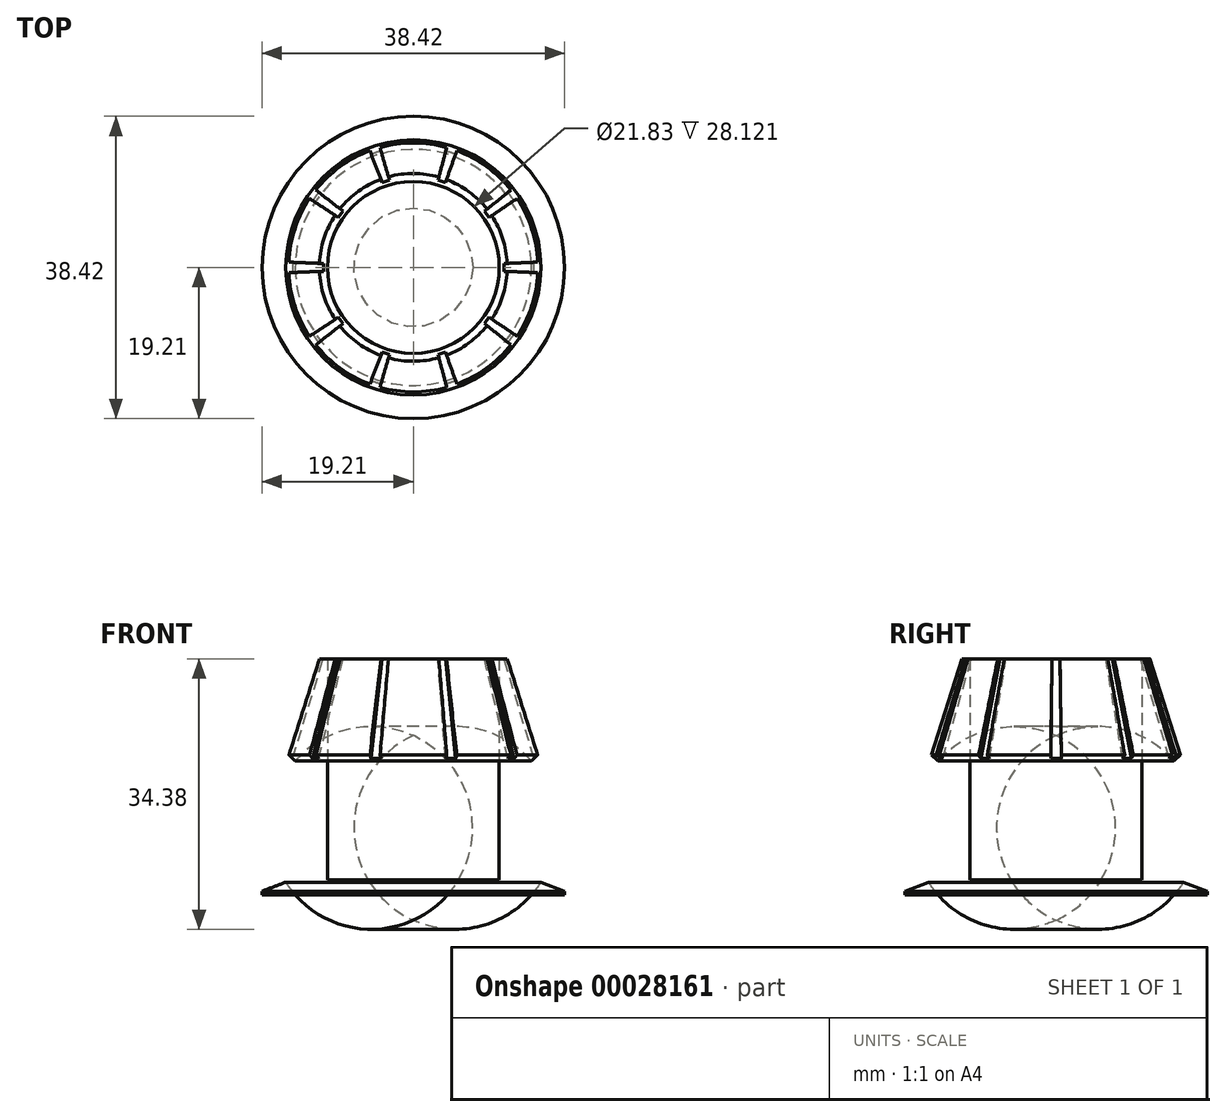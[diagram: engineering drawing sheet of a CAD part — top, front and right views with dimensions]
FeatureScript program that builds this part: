
annotation { "Feature Type Name" : "Feature", "Feature Type Description" : "" }
export const myFeature = defineFeature(function(context is Context, id is Id, definition is map)
    precondition{}
    {
        {
            var Q0;
            Q0=qCreatedBy(makeId("Front.planeOp"),FACE);
            var sketch = newSketch(context, id + "F0", { "sketchPlane" : qUnion([Q0])});
            skLineSegment(sketch, "E0", {"start": v(0, 0) * mm, "end": v(0, 30) * mm});
            skLineSegment(sketch, "E1", {"start": v(0, 0) * mm, "end": v(15, 0) * mm});
            skLineSegment(sketch, "E2", {"start": v(15, 0) * mm, "end": v(15, 17) * mm});
            skArc(sketch, "E3", {"start": v(15, 0) * mm, "mid": v(18.2, 8.5) * mm, "end": v(15, 17) * mm});
            skLineSegment(sketch, "E4", {"start": v(16.2, 1.6) * mm, "end": v(19.2, 0.46) * mm});
            skLineSegment(sketch, "E5", {"start": v(19.2, 0.46) * mm, "end": v(19.2, 0) * mm});
            skLineSegment(sketch, "E6", {"start": v(19.2, 0) * mm, "end": v(15, 0) * mm});
            skLineSegment(sketch, "E7", {"start": v(15, 17) * mm, "end": v(15.81, 17.76) * mm});
            skLineSegment(sketch, "E8", {"start": v(15.81, 17.76) * mm, "end": v(11.93, 30) * mm});
            skLineSegment(sketch, "E9", {"start": v(11.93, 30) * mm, "end": v(10.91, 30) * mm});
            skLineSegment(sketch, "E10", {"start": v(10.91, 30) * mm, "end": v(10.91, 1.88) * mm});
            skLineSegment(sketch, "E11", {"start": v(10.91, 1.88) * mm, "end": v(0, 1.88) * mm});
            skSolve(sketch);
        }
        {
            var Q0;
            Q0 = qSketchRegion(id + "F0", true);
            var Q1;
            Q1=sQuery(id+"F0.wireOp",EDGE,"E0");
            revolve(context, id + "F1", {"entities" : qUnion([Q0]), "axis" : qUnion([Q1]), "revolveType" : RevolveType.FULL});
        }
        {
            var Q0;
            Q0=makeQuery(id+"F1.opRevolve","SWEPT_FACE",FACE,{"disambiguationData":[OSD([sQuery(id+"F0.wireOp",EDGE,"E9")])]});
            var sketch = newSketch(context, id + "F2", { "sketchPlane" : qUnion([Q0])});
            skLineSegment(sketch, "E12.rect.bottom", {"start": v(12.33, 0.5) * mm, "end": v(11.53, 0.5) * mm});
            skLineSegment(sketch, "E12.rect.top", {"start": v(12.33, -0.5) * mm, "end": v(11.53, -0.5) * mm});
            skLineSegment(sketch, "E12.rect.left", {"start": v(12.33, 0.5) * mm, "end": v(12.33, -0.5) * mm});
            skLineSegment(sketch, "E12.rect.right", {"start": v(11.53, 0.5) * mm, "end": v(11.53, -0.5) * mm});
            skPoint(sketch, "E12.rect.middle", {"position": v(11.93, 0) * mm});
            skPoint(sketch, "E13.1.0", {"position": v(9.66, 6.98) * mm});
            skLineSegment(sketch, "E13.1.1", {"start": v(9.68, 7.63) * mm, "end": v(9.04, 7.16) * mm});
            skLineSegment(sketch, "E13.1.2", {"start": v(10.28, 6.8) * mm, "end": v(9.64, 6.33) * mm});
            skLineSegment(sketch, "E13.1.3", {"start": v(9.68, 7.63) * mm, "end": v(10.28, 6.8) * mm});
            skLineSegment(sketch, "E13.1.4", {"start": v(9.04, 7.16) * mm, "end": v(9.64, 6.33) * mm});
            skPoint(sketch, "E13.2.0", {"position": v(3.72, 11.3) * mm});
            skLineSegment(sketch, "E13.2.1", {"start": v(3.36, 11.83) * mm, "end": v(3.11, 11.07) * mm});
            skLineSegment(sketch, "E13.2.2", {"start": v(4.33, 11.52) * mm, "end": v(4.08, 10.76) * mm});
            skLineSegment(sketch, "E13.2.3", {"start": v(3.36, 11.83) * mm, "end": v(4.33, 11.52) * mm});
            skLineSegment(sketch, "E13.2.4", {"start": v(3.11, 11.07) * mm, "end": v(4.08, 10.76) * mm});
            skPoint(sketch, "E13.3.0", {"position": v(-3.62, 11.3) * mm});
            skLineSegment(sketch, "E13.3.1", {"start": v(-4.23, 11.52) * mm, "end": v(-3.98, 10.76) * mm});
            skLineSegment(sketch, "E13.3.2", {"start": v(-3.26, 11.83) * mm, "end": v(-3.01, 11.07) * mm});
            skLineSegment(sketch, "E13.3.3", {"start": v(-4.23, 11.52) * mm, "end": v(-3.26, 11.83) * mm});
            skLineSegment(sketch, "E13.3.4", {"start": v(-3.98, 10.76) * mm, "end": v(-3.01, 11.07) * mm});
            skPoint(sketch, "E13.4.0", {"position": v(-9.56, 6.98) * mm});
            skLineSegment(sketch, "E13.4.1", {"start": v(-10.18, 6.8) * mm, "end": v(-9.53, 6.33) * mm});
            skLineSegment(sketch, "E13.4.2", {"start": v(-9.58, 7.63) * mm, "end": v(-8.93, 7.16) * mm});
            skLineSegment(sketch, "E13.4.3", {"start": v(-10.18, 6.8) * mm, "end": v(-9.58, 7.63) * mm});
            skLineSegment(sketch, "E13.4.4", {"start": v(-9.53, 6.33) * mm, "end": v(-8.93, 7.16) * mm});
            skPoint(sketch, "E13.5.0", {"position": v(-11.83, 0) * mm});
            skLineSegment(sketch, "E13.5.1", {"start": v(-12.23, -0.5) * mm, "end": v(-11.43, -0.5) * mm});
            skLineSegment(sketch, "E13.5.2", {"start": v(-12.23, 0.5) * mm, "end": v(-11.43, 0.5) * mm});
            skLineSegment(sketch, "E13.5.3", {"start": v(-12.23, -0.5) * mm, "end": v(-12.23, 0.5) * mm});
            skLineSegment(sketch, "E13.5.4", {"start": v(-11.43, -0.5) * mm, "end": v(-11.43, 0.5) * mm});
            skPoint(sketch, "E13.6.0", {"position": v(-9.56, -6.98) * mm});
            skLineSegment(sketch, "E13.6.1", {"start": v(-9.58, -7.63) * mm, "end": v(-8.93, -7.16) * mm});
            skLineSegment(sketch, "E13.6.2", {"start": v(-10.18, -6.8) * mm, "end": v(-9.53, -6.33) * mm});
            skLineSegment(sketch, "E13.6.3", {"start": v(-9.58, -7.63) * mm, "end": v(-10.18, -6.8) * mm});
            skLineSegment(sketch, "E13.6.4", {"start": v(-8.93, -7.16) * mm, "end": v(-9.53, -6.33) * mm});
            skPoint(sketch, "E13.7.0", {"position": v(-3.62, -11.3) * mm});
            skLineSegment(sketch, "E13.7.1", {"start": v(-3.26, -11.83) * mm, "end": v(-3.01, -11.07) * mm});
            skLineSegment(sketch, "E13.7.2", {"start": v(-4.23, -11.52) * mm, "end": v(-3.98, -10.76) * mm});
            skLineSegment(sketch, "E13.7.3", {"start": v(-3.26, -11.83) * mm, "end": v(-4.23, -11.52) * mm});
            skLineSegment(sketch, "E13.7.4", {"start": v(-3.01, -11.07) * mm, "end": v(-3.98, -10.76) * mm});
            skPoint(sketch, "E13.8.0", {"position": v(3.72, -11.3) * mm});
            skLineSegment(sketch, "E13.8.1", {"start": v(4.33, -11.52) * mm, "end": v(4.08, -10.76) * mm});
            skLineSegment(sketch, "E13.8.2", {"start": v(3.36, -11.83) * mm, "end": v(3.11, -11.07) * mm});
            skLineSegment(sketch, "E13.8.3", {"start": v(4.33, -11.52) * mm, "end": v(3.36, -11.83) * mm});
            skLineSegment(sketch, "E13.8.4", {"start": v(4.08, -10.76) * mm, "end": v(3.11, -11.07) * mm});
            skPoint(sketch, "E13.9.0", {"position": v(9.66, -6.98) * mm});
            skLineSegment(sketch, "E13.9.1", {"start": v(10.28, -6.8) * mm, "end": v(9.64, -6.33) * mm});
            skLineSegment(sketch, "E13.9.2", {"start": v(9.68, -7.63) * mm, "end": v(9.04, -7.16) * mm});
            skLineSegment(sketch, "E13.9.3", {"start": v(10.28, -6.8) * mm, "end": v(9.68, -7.63) * mm});
            skLineSegment(sketch, "E13.9.4", {"start": v(9.64, -6.33) * mm, "end": v(9.04, -7.16) * mm});
            skPoint(sketch, "E13.center", {"position": v(0.05, 0) * mm});
            skSolve(sketch);
        }
        {
            var Q0;
            Q0=qCreatedBy(makeId("Top.planeOp"),FACE);
            cPlane(context, id + "F3", {"entities" : qUnion([Q0]), "cplaneType" : CPlaneType.OFFSET, "offset" : 17 * mm, "width" : 150 * mm, "height" : 150 * mm});
        }
        {
            var Q0;
            Q0=qCreatedBy(id+"F3.planeOp",FACE);
            var sketch = newSketch(context, id + "F4", { "sketchPlane" : qUnion([Q0])});
            skLineSegment(sketch, "E14.rect.bottom", {"start": v(15.44, 0.68) * mm, "end": v(16.24, 0.68) * mm});
            skLineSegment(sketch, "E14.rect.top", {"start": v(15.44, -0.68) * mm, "end": v(16.24, -0.68) * mm});
            skLineSegment(sketch, "E14.rect.left", {"start": v(15.44, 0.68) * mm, "end": v(15.44, -0.68) * mm});
            skLineSegment(sketch, "E14.rect.right", {"start": v(16.24, 0.68) * mm, "end": v(16.24, -0.68) * mm});
            skPoint(sketch, "E14.rect.middle", {"position": v(15.84, 0) * mm});
            skLineSegment(sketch, "E15.1.0", {"start": v(12.09, 9.63) * mm, "end": v(12.73, 10.1) * mm});
            skLineSegment(sketch, "E15.1.1", {"start": v(12.89, 8.52) * mm, "end": v(13.54, 9) * mm});
            skLineSegment(sketch, "E15.1.2", {"start": v(12.09, 9.63) * mm, "end": v(12.89, 8.52) * mm});
            skLineSegment(sketch, "E15.1.3", {"start": v(12.73, 10.1) * mm, "end": v(13.54, 9) * mm});
            skPoint(sketch, "E15.1.8", {"position": v(12.81, 9.3) * mm});
            skLineSegment(sketch, "E15.2.0", {"start": v(4.12, 14.9) * mm, "end": v(4.37, 15.65) * mm});
            skLineSegment(sketch, "E15.2.1", {"start": v(5.42, 14.47) * mm, "end": v(5.67, 15.23) * mm});
            skLineSegment(sketch, "E15.2.2", {"start": v(4.12, 14.9) * mm, "end": v(5.42, 14.47) * mm});
            skLineSegment(sketch, "E15.2.3", {"start": v(4.37, 15.65) * mm, "end": v(5.67, 15.23) * mm});
            skPoint(sketch, "E15.2.8", {"position": v(4.9, 15.06) * mm});
            skLineSegment(sketch, "E15.3.0", {"start": v(-5.42, 14.47) * mm, "end": v(-5.67, 15.23) * mm});
            skLineSegment(sketch, "E15.3.1", {"start": v(-4.12, 14.9) * mm, "end": v(-4.37, 15.65) * mm});
            skLineSegment(sketch, "E15.3.2", {"start": v(-5.42, 14.47) * mm, "end": v(-4.12, 14.9) * mm});
            skLineSegment(sketch, "E15.3.3", {"start": v(-5.67, 15.23) * mm, "end": v(-4.37, 15.65) * mm});
            skPoint(sketch, "E15.3.8", {"position": v(-4.9, 15.06) * mm});
            skLineSegment(sketch, "E15.4.0", {"start": v(-12.89, 8.52) * mm, "end": v(-13.54, 9) * mm});
            skLineSegment(sketch, "E15.4.1", {"start": v(-12.09, 9.63) * mm, "end": v(-12.73, 10.1) * mm});
            skLineSegment(sketch, "E15.4.2", {"start": v(-12.89, 8.52) * mm, "end": v(-12.09, 9.63) * mm});
            skLineSegment(sketch, "E15.4.3", {"start": v(-13.54, 9) * mm, "end": v(-12.73, 10.1) * mm});
            skPoint(sketch, "E15.4.8", {"position": v(-12.81, 9.3) * mm});
            skLineSegment(sketch, "E15.5.0", {"start": v(-15.44, -0.68) * mm, "end": v(-16.24, -0.68) * mm});
            skLineSegment(sketch, "E15.5.1", {"start": v(-15.44, 0.68) * mm, "end": v(-16.24, 0.68) * mm});
            skLineSegment(sketch, "E15.5.2", {"start": v(-15.44, -0.68) * mm, "end": v(-15.44, 0.68) * mm});
            skLineSegment(sketch, "E15.5.3", {"start": v(-16.24, -0.68) * mm, "end": v(-16.24, 0.68) * mm});
            skPoint(sketch, "E15.5.8", {"position": v(-15.84, 0) * mm});
            skLineSegment(sketch, "E15.6.0", {"start": v(-12.09, -9.63) * mm, "end": v(-12.73, -10.1) * mm});
            skLineSegment(sketch, "E15.6.1", {"start": v(-12.89, -8.52) * mm, "end": v(-13.54, -9) * mm});
            skLineSegment(sketch, "E15.6.2", {"start": v(-12.09, -9.63) * mm, "end": v(-12.89, -8.52) * mm});
            skLineSegment(sketch, "E15.6.3", {"start": v(-12.73, -10.1) * mm, "end": v(-13.54, -9) * mm});
            skPoint(sketch, "E15.6.8", {"position": v(-12.81, -9.3) * mm});
            skLineSegment(sketch, "E15.7.0", {"start": v(-4.12, -14.9) * mm, "end": v(-4.37, -15.65) * mm});
            skLineSegment(sketch, "E15.7.1", {"start": v(-5.42, -14.47) * mm, "end": v(-5.67, -15.23) * mm});
            skLineSegment(sketch, "E15.7.2", {"start": v(-4.12, -14.9) * mm, "end": v(-5.42, -14.47) * mm});
            skLineSegment(sketch, "E15.7.3", {"start": v(-4.37, -15.65) * mm, "end": v(-5.67, -15.23) * mm});
            skPoint(sketch, "E15.7.8", {"position": v(-4.9, -15.06) * mm});
            skLineSegment(sketch, "E15.8.0", {"start": v(5.42, -14.47) * mm, "end": v(5.67, -15.23) * mm});
            skLineSegment(sketch, "E15.8.1", {"start": v(4.12, -14.9) * mm, "end": v(4.37, -15.65) * mm});
            skLineSegment(sketch, "E15.8.2", {"start": v(5.42, -14.47) * mm, "end": v(4.12, -14.9) * mm});
            skLineSegment(sketch, "E15.8.3", {"start": v(5.67, -15.23) * mm, "end": v(4.37, -15.65) * mm});
            skPoint(sketch, "E15.8.8", {"position": v(4.9, -15.06) * mm});
            skLineSegment(sketch, "E15.9.0", {"start": v(12.89, -8.52) * mm, "end": v(13.54, -9) * mm});
            skLineSegment(sketch, "E15.9.1", {"start": v(12.09, -9.63) * mm, "end": v(12.73, -10.1) * mm});
            skLineSegment(sketch, "E15.9.2", {"start": v(12.89, -8.52) * mm, "end": v(12.09, -9.63) * mm});
            skLineSegment(sketch, "E15.9.3", {"start": v(13.54, -9) * mm, "end": v(12.73, -10.1) * mm});
            skPoint(sketch, "E15.9.8", {"position": v(12.81, -9.3) * mm});
            skPoint(sketch, "E15.center", {"position": v(0, 0) * mm});
            skSolve(sketch);
        }
        {
            var Q1;
            Q1=makeQuery(id+"F4.imprint","IMPRINT",FACE,{"disambiguationData":[TD([[makeQuery(id+"F4.imprint","IMPRINT",EDGE,{"derivedFrom":sQuery(id+"F4.wireOp",EDGE,"E14.rect.bottom")}),-1.0]])]});
            var Q2;
            {var subQ5=sQuery(id+"F2.wireOp",EDGE,"E12.rect.right");Q2=makeQuery(id+"F2.imprint","IMPRINT",FACE,{"disambiguationData":[TD([[makeQuery(id+"F2.imprint","IMPRINT",EDGE,{"derivedFrom":subQ5}),1.0]])]});}
            loft(context, id + "F5", {"operationType" : NewBodyOperationType.REMOVE, "sheetProfilesArray" : [{ "sheetProfileEntities" : qUnion([Q1]) }, { "sheetProfileEntities" : qUnion([Q2]) }]});
        }
        {
            var Q1;
            Q1=makeQuery(id+"F4.imprint","IMPRINT",FACE,{"disambiguationData":[TD([[makeQuery(id+"F4.imprint","IMPRINT",EDGE,{"derivedFrom":sQuery(id+"F4.wireOp",EDGE,"E15.1.0")}),-1.0]])]});
            var Q2;
            {var subQ5=sQuery(id+"F2.wireOp",EDGE,"E13.1.4");Q2=makeQuery(id+"F2.imprint","IMPRINT",FACE,{"disambiguationData":[TD([[makeQuery(id+"F2.imprint","IMPRINT",EDGE,{"derivedFrom":subQ5}),1.0]])]});}
            loft(context, id + "F6", {"operationType" : NewBodyOperationType.REMOVE, "sheetProfilesArray" : [{ "sheetProfileEntities" : qUnion([Q1]) }, { "sheetProfileEntities" : qUnion([Q2]) }]});
        }
        {
            var Q1;
            Q1=makeQuery(id+"F4.imprint","IMPRINT",FACE,{"disambiguationData":[TD([[makeQuery(id+"F4.imprint","IMPRINT",EDGE,{"derivedFrom":sQuery(id+"F4.wireOp",EDGE,"E15.2.0")}),-1.0]])]});
            var Q2;
            {var subQ5=sQuery(id+"F2.wireOp",EDGE,"E13.2.4");Q2=makeQuery(id+"F2.imprint","IMPRINT",FACE,{"disambiguationData":[TD([[makeQuery(id+"F2.imprint","IMPRINT",EDGE,{"derivedFrom":subQ5}),1.0]])]});}
            loft(context, id + "F7", {"operationType" : NewBodyOperationType.REMOVE, "sheetProfilesArray" : [{ "sheetProfileEntities" : qUnion([Q1]) }, { "sheetProfileEntities" : qUnion([Q2]) }]});
        }
        {
            var Q1;
            Q1=makeQuery(id+"F4.imprint","IMPRINT",FACE,{"disambiguationData":[TD([[makeQuery(id+"F4.imprint","IMPRINT",EDGE,{"derivedFrom":sQuery(id+"F4.wireOp",EDGE,"E15.3.0")}),-1.0]])]});
            var Q2;
            {var subQ5=sQuery(id+"F2.wireOp",EDGE,"E13.3.4");Q2=makeQuery(id+"F2.imprint","IMPRINT",FACE,{"disambiguationData":[TD([[makeQuery(id+"F2.imprint","IMPRINT",EDGE,{"derivedFrom":subQ5}),1.0]])]});}
            loft(context, id + "F8", {"operationType" : NewBodyOperationType.REMOVE, "sheetProfilesArray" : [{ "sheetProfileEntities" : qUnion([Q1]) }, { "sheetProfileEntities" : qUnion([Q2]) }]});
        }
        {
            var Q1;
            Q1=makeQuery(id+"F4.imprint","IMPRINT",FACE,{"disambiguationData":[TD([[makeQuery(id+"F4.imprint","IMPRINT",EDGE,{"derivedFrom":sQuery(id+"F4.wireOp",EDGE,"E15.4.0")}),-1.0]])]});
            var Q2;
            {var subQ5=sQuery(id+"F2.wireOp",EDGE,"E13.4.4");Q2=makeQuery(id+"F2.imprint","IMPRINT",FACE,{"disambiguationData":[TD([[makeQuery(id+"F2.imprint","IMPRINT",EDGE,{"derivedFrom":subQ5}),1.0]])]});}
            loft(context, id + "F9", {"operationType" : NewBodyOperationType.REMOVE, "sheetProfilesArray" : [{ "sheetProfileEntities" : qUnion([Q1]) }, { "sheetProfileEntities" : qUnion([Q2]) }]});
        }
        {
            var Q1;
            Q1=makeQuery(id+"F4.imprint","IMPRINT",FACE,{"disambiguationData":[TD([[makeQuery(id+"F4.imprint","IMPRINT",EDGE,{"derivedFrom":sQuery(id+"F4.wireOp",EDGE,"E15.5.0")}),-1.0]])]});
            var Q2;
            {var subQ5=sQuery(id+"F2.wireOp",EDGE,"E13.5.4");Q2=makeQuery(id+"F2.imprint","IMPRINT",FACE,{"disambiguationData":[TD([[makeQuery(id+"F2.imprint","IMPRINT",EDGE,{"derivedFrom":subQ5}),1.0]])]});}
            loft(context, id + "F10", {"operationType" : NewBodyOperationType.REMOVE, "sheetProfilesArray" : [{ "sheetProfileEntities" : qUnion([Q1]) }, { "sheetProfileEntities" : qUnion([Q2]) }]});
        }
        {
            var Q1;
            Q1=makeQuery(id+"F4.imprint","IMPRINT",FACE,{"disambiguationData":[TD([[makeQuery(id+"F4.imprint","IMPRINT",EDGE,{"derivedFrom":sQuery(id+"F4.wireOp",EDGE,"E15.6.0")}),-1.0]])]});
            var Q2;
            {var subQ5=sQuery(id+"F2.wireOp",EDGE,"E13.6.4");Q2=makeQuery(id+"F2.imprint","IMPRINT",FACE,{"disambiguationData":[TD([[makeQuery(id+"F2.imprint","IMPRINT",EDGE,{"derivedFrom":subQ5}),1.0]])]});}
            loft(context, id + "F11", {"operationType" : NewBodyOperationType.REMOVE, "sheetProfilesArray" : [{ "sheetProfileEntities" : qUnion([Q1]) }, { "sheetProfileEntities" : qUnion([Q2]) }]});
        }
        {
            var Q1;
            Q1=makeQuery(id+"F4.imprint","IMPRINT",FACE,{"disambiguationData":[TD([[makeQuery(id+"F4.imprint","IMPRINT",EDGE,{"derivedFrom":sQuery(id+"F4.wireOp",EDGE,"E15.7.0")}),-1.0]])]});
            var Q2;
            {var subQ5=sQuery(id+"F2.wireOp",EDGE,"E13.7.4");Q2=makeQuery(id+"F2.imprint","IMPRINT",FACE,{"disambiguationData":[TD([[makeQuery(id+"F2.imprint","IMPRINT",EDGE,{"derivedFrom":subQ5}),1.0]])]});}
            loft(context, id + "F12", {"operationType" : NewBodyOperationType.REMOVE, "sheetProfilesArray" : [{ "sheetProfileEntities" : qUnion([Q1]) }, { "sheetProfileEntities" : qUnion([Q2]) }]});
        }
        {
            var Q1;
            Q1=makeQuery(id+"F4.imprint","IMPRINT",FACE,{"disambiguationData":[TD([[makeQuery(id+"F4.imprint","IMPRINT",EDGE,{"derivedFrom":sQuery(id+"F4.wireOp",EDGE,"E15.8.0")}),-1.0]])]});
            var Q2;
            {var subQ0=sQuery(id+"F2.wireOp",EDGE,"E13.8.4");Q2=makeQuery(id+"F2.imprint","IMPRINT",FACE,{"disambiguationData":[TD([[makeQuery(id+"F2.imprint","IMPRINT",EDGE,{"derivedFrom":subQ0}),1.0]])]});}
            loft(context, id + "F13", {"operationType" : NewBodyOperationType.REMOVE, "sheetProfilesArray" : [{ "sheetProfileEntities" : qUnion([Q1]) }, { "sheetProfileEntities" : qUnion([Q2]) }]});
        }
        {
            var Q1;
            Q1=makeQuery(id+"F4.imprint","IMPRINT",FACE,{"disambiguationData":[TD([[makeQuery(id+"F4.imprint","IMPRINT",EDGE,{"derivedFrom":sQuery(id+"F4.wireOp",EDGE,"E15.9.0")}),-1.0]])]});
            var Q2;
            {var subQ5=sQuery(id+"F2.wireOp",EDGE,"E13.9.4");Q2=makeQuery(id+"F2.imprint","IMPRINT",FACE,{"disambiguationData":[TD([[makeQuery(id+"F2.imprint","IMPRINT",EDGE,{"derivedFrom":subQ5}),1.0]])]});}
            loft(context, id + "F14", {"operationType" : NewBodyOperationType.REMOVE, "sheetProfilesArray" : [{ "sheetProfileEntities" : qUnion([Q1]) }, { "sheetProfileEntities" : qUnion([Q2]) }]});
        }
    });
